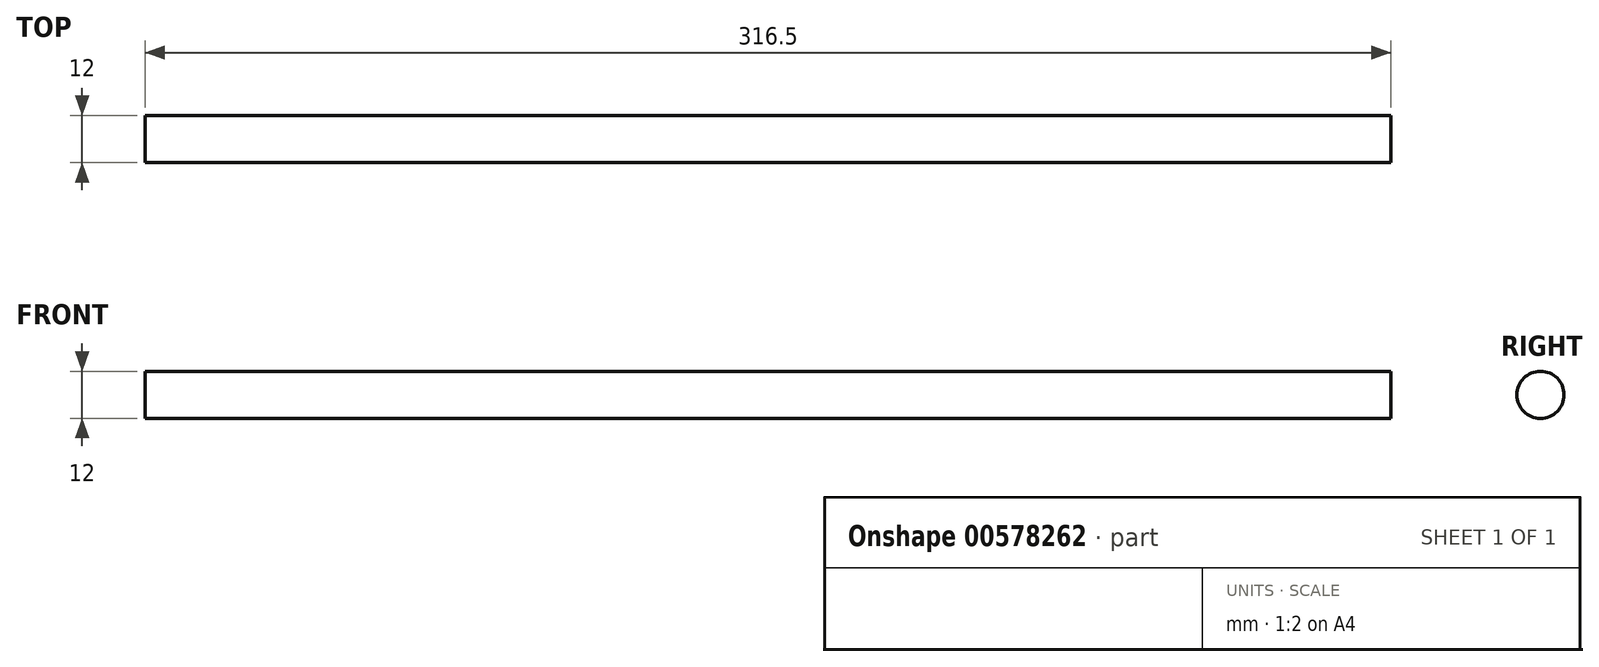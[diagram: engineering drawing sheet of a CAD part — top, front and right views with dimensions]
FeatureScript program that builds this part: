
annotation { "Feature Type Name" : "Feature", "Feature Type Description" : "" }
export const myFeature = defineFeature(function(context is Context, id is Id, definition is map)
    precondition{}
    {
        {
            var Q0;
            Q0=qCreatedBy(makeId("Right.planeOp"),FACE);
            var sketch = newSketch(context, id + "F0", { "sketchPlane" : qUnion([Q0])});
            skCircle(sketch, "E0", {"center": v(0, 0) * mm, "radius": 6 * mm});
            skSolve(sketch);
        }
        {
            var Q0;
            Q0 = qSketchRegion(id + "F0", true);
            extrude(context, id + "F1", {"entities" : qUnion([Q0]), "depth" : 316.5 * mm, "offsetDistance" : 25 * mm});
        }
    });
